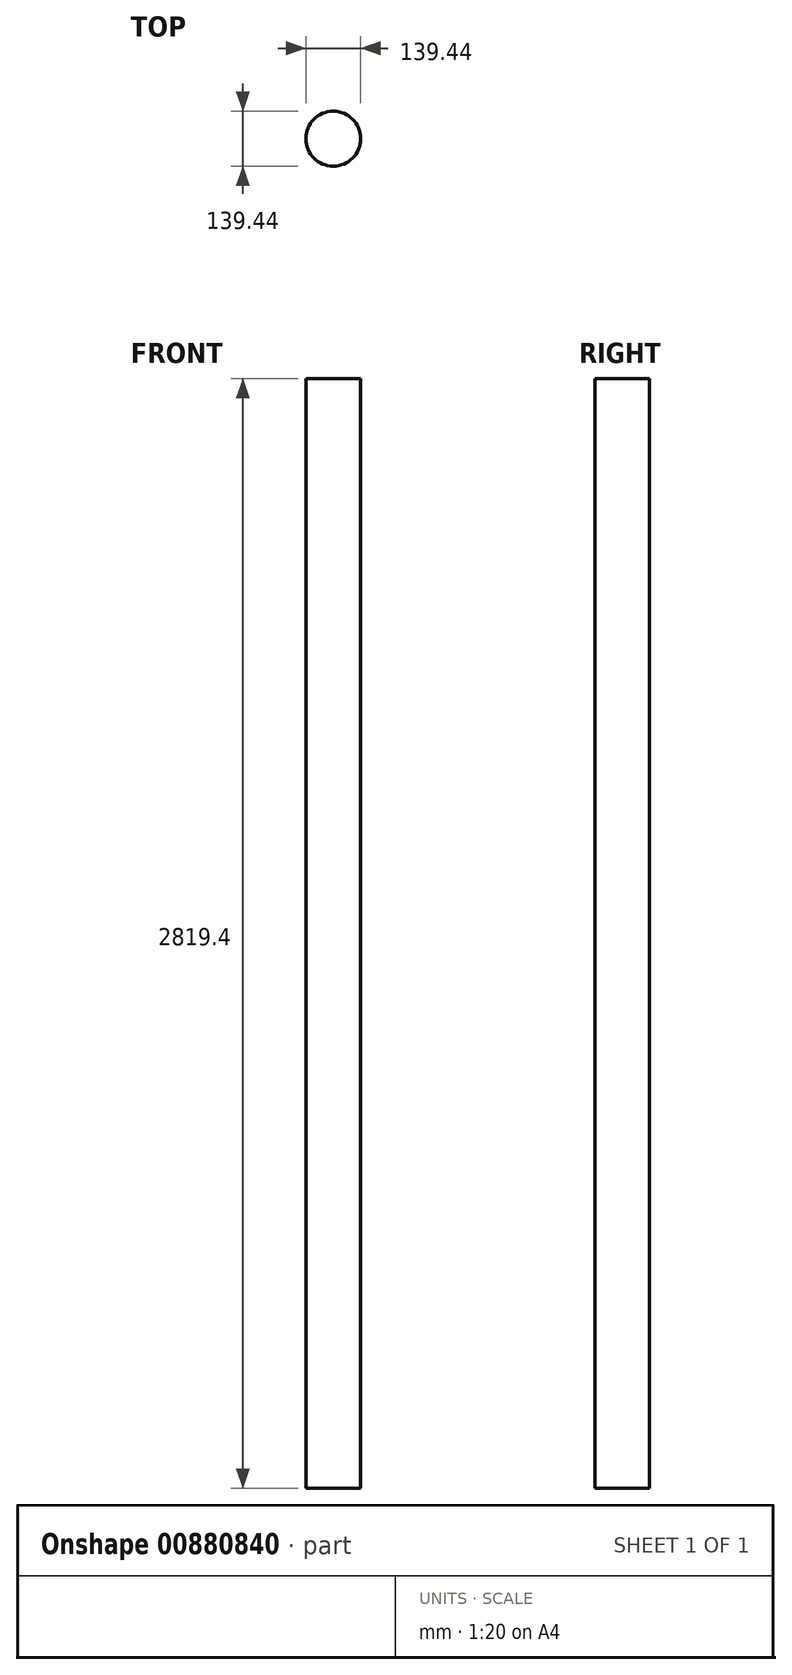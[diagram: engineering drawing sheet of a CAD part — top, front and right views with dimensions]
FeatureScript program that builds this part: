
annotation { "Feature Type Name" : "Feature", "Feature Type Description" : "" }
export const myFeature = defineFeature(function(context is Context, id is Id, definition is map)
    precondition{}
    {
        {
            var Q0;
            Q0=qCreatedBy(makeId("Top.planeOp"),FACE);
            var sketch = newSketch(context, id + "F0", { "sketchPlane" : qUnion([Q0])});
            skCircle(sketch, "E0", {"center": v(0, 0) * mm, "radius": 69.72 * mm});
            skSolve(sketch);
        }
        {
            var Q0;
            Q0 = qSketchRegion(id + "F0", true);
            extrude(context, id + "F1", {"entities" : qUnion([Q0]), "depth" : 2819.4 * mm, "offsetDistance" : 25.4 * mm});
        }
    });
